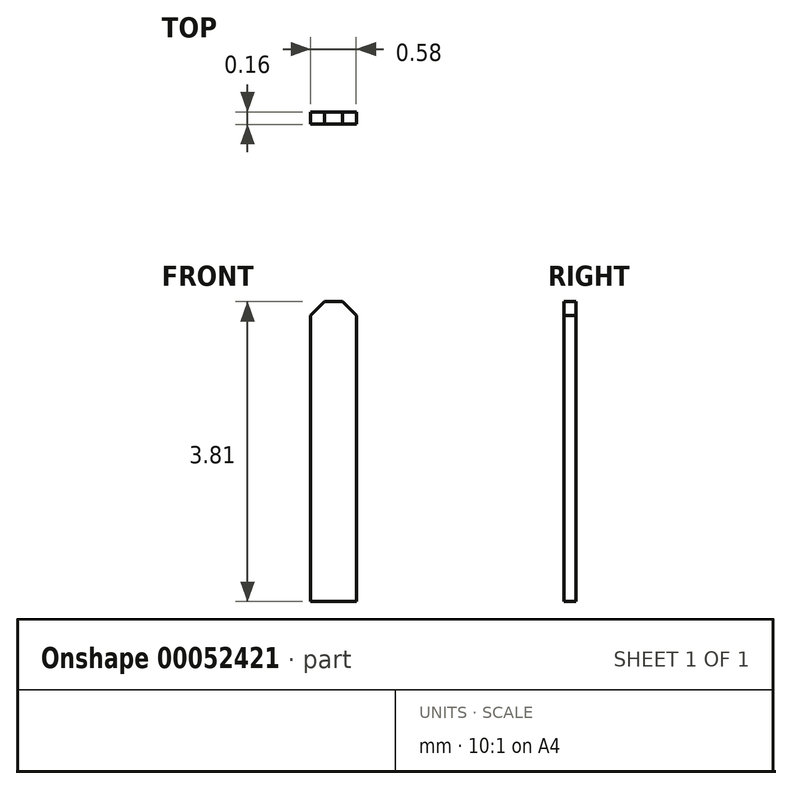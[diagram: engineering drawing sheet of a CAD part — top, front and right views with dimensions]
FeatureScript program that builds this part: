
annotation { "Feature Type Name" : "Feature", "Feature Type Description" : "" }
export const myFeature = defineFeature(function(context is Context, id is Id, definition is map)
    precondition{}
    {
        {
            var Q0;
            Q0=qCreatedBy(makeId("Top.planeOp"),FACE);
            var sketch = newSketch(context, id + "F0", { "sketchPlane" : qUnion([Q0])});
            skLineSegment(sketch, "E0.rect.bottom", {"start": v(0.3, -0.08) * mm, "end": v(-0.3, -0.08) * mm});
            skLineSegment(sketch, "E0.rect.top", {"start": v(0.3, 0.08) * mm, "end": v(-0.3, 0.08) * mm});
            skLineSegment(sketch, "E0.rect.left", {"start": v(0.3, -0.08) * mm, "end": v(0.3, 0.08) * mm});
            skLineSegment(sketch, "E0.rect.right", {"start": v(-0.3, -0.08) * mm, "end": v(-0.3, 0.08) * mm});
            skPoint(sketch, "E0.rect.middle", {"position": v(0, 0) * mm});
            skSolve(sketch);
        }
        {
            var Q0;
            Q0 = qSketchRegion(id + "F0", true);
            extrude(context, id + "F1", {"entities" : qUnion([Q0]), "depth" : 3.8 * mm});
        }
        {
            var Q0;
            Q0=makeQuery(id+"F1.opExtrude","CAP_EDGE",EDGE,{"disambiguationData":[OSD([sQuery(id+"F0.wireOp",EDGE,"E0.rect.right")])],"isStart":false});
            var Q1;
            Q1=makeQuery(id+"F1.opExtrude","CAP_EDGE",EDGE,{"disambiguationData":[OSD([sQuery(id+"F0.wireOp",EDGE,"E0.rect.left")])],"isStart":false});
            chamfer(context, id + "F2", {"entities" : qUnion([Q0, Q1]), "width" : 0.18 * mm, "tangentPropagation" : true});
        }
    });
